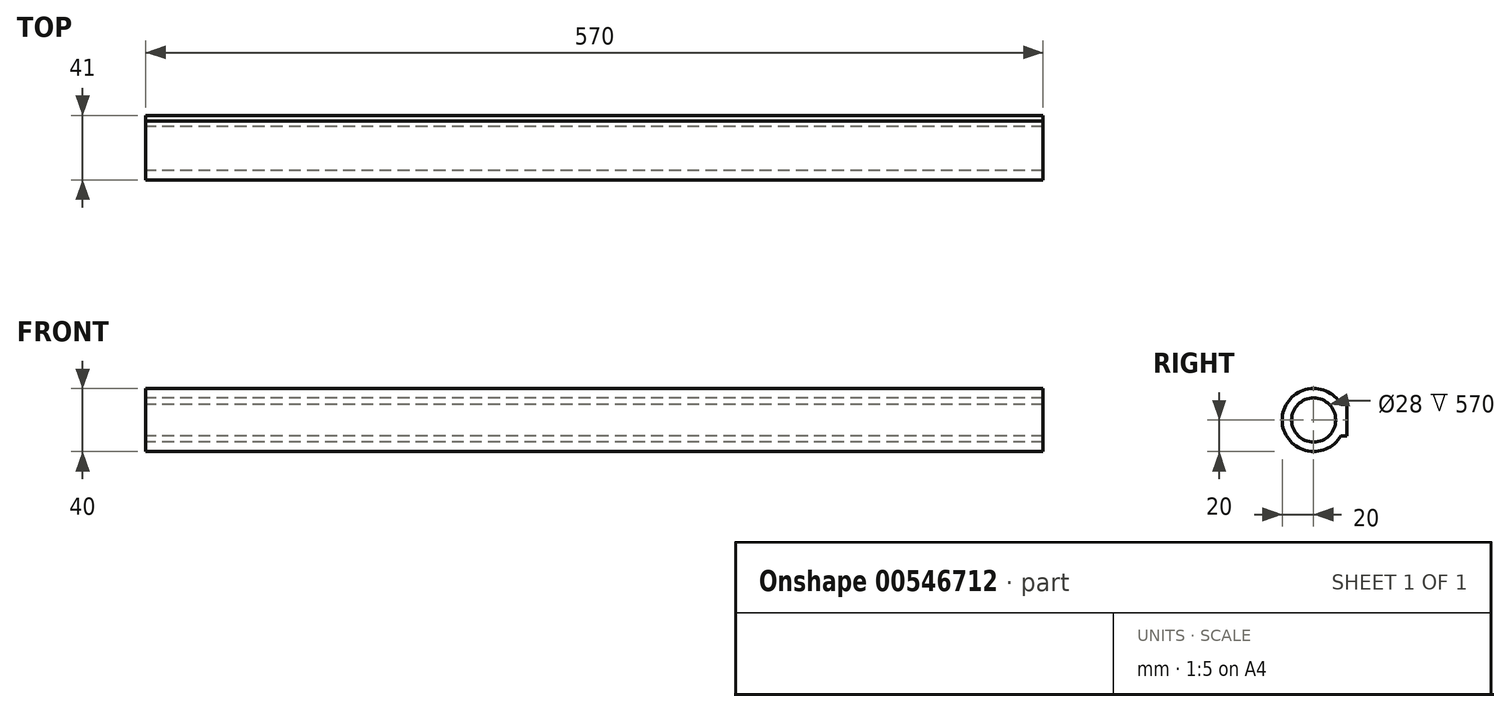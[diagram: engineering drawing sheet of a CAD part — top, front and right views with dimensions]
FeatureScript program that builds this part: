
annotation { "Feature Type Name" : "Feature", "Feature Type Description" : "" }
export const myFeature = defineFeature(function(context is Context, id is Id, definition is map)
    precondition{}
    {
        {
            var Q0;
            Q0=qCreatedBy(makeId("Right.planeOp"),FACE);
            var sketch = newSketch(context, id + "F0", { "sketchPlane" : qUnion([Q0])});
            skArc(sketch, "E0", {"start": v(17.32, 10) * mm, "mid": v(-20, 0) * mm, "end": v(17.32, -10) * mm});
            skCircle(sketch, "E1", {"center": v(0, 0) * mm, "radius": 14 * mm});
            skLineSegment(sketch, "E2.bottom", {"start": v(21, 10) * mm, "end": v(17, 10) * mm});
            skLineSegment(sketch, "E2.top", {"start": v(21, -10) * mm, "end": v(17, -10) * mm});
            skLineSegment(sketch, "E2.left", {"start": v(21, 10) * mm, "end": v(21, -10) * mm});
            skSolve(sketch);
        }
        {
            var Q0;
            Q0=makeQuery(id+"F0.imprint","IMPRINT",FACE,{"disambiguationData":[TD([[makeQuery(id+"F0.imprint","IMPRINT",EDGE,{"derivedFrom":sQuery(id+"F0.wireOp",EDGE,"E0")}),1.0]])]});
            extrude(context, id + "F1", {"entities" : qUnion([Q0]), "depth" : 570 * mm, "offsetDistance" : 25 * mm});
        }
    });
